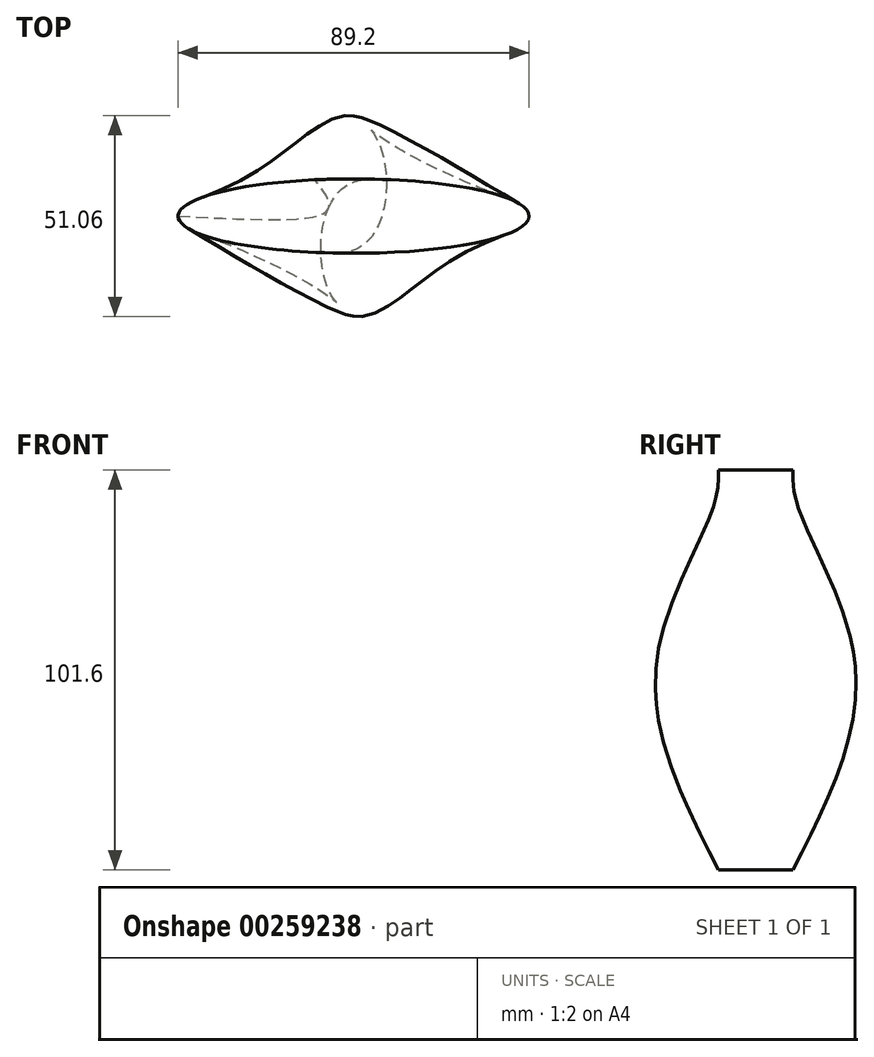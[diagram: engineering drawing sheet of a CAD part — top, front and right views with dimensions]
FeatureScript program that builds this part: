
annotation { "Feature Type Name" : "Feature", "Feature Type Description" : "" }
export const myFeature = defineFeature(function(context is Context, id is Id, definition is map)
    precondition{}
    {
        {
            var Q0;
            Q0=qCreatedBy(makeId("Top.planeOp"),FACE);
            var sketch = newSketch(context, id + "F0", { "sketchPlane" : qUnion([Q0])});
            skEllipse(sketch, "E0", {"center": v(0, 0) * mm, "majorRadius": 44.6 * mm, "minorRadius": 9.45 * mm, "majorAxis": v(-1, 0)});
            skSolve(sketch);
        }
        {
            var Q0;
            Q0=qCreatedBy(makeId("Top.planeOp"),FACE);
            cPlane(context, id + "F1", {"entities" : qUnion([Q0]), "cplaneType" : CPlaneType.OFFSET, "offset" : 50.8 * mm, "width" : 152.4 * mm, "height" : 152.4 * mm});
        }
        {
            var Q0;
            Q0=qCreatedBy(id+"F1.planeOp",FACE);
            var sketch = newSketch(context, id + "F2", { "sketchPlane" : qUnion([Q0])});
            skEllipse(sketch, "E1.0", {"center": v(0, 0) * mm, "majorRadius": 25.4 * mm, "minorRadius": 9.45 * mm, "majorAxis": v(0, 1)});
            skEllipse(sketch, "E2.0.0", {"center": v(0, 0) * mm, "majorRadius": 44.6 * mm, "minorRadius": 9.45 * mm, "majorAxis": v(-1, 0), "construction": true});
            skSolve(sketch);
        }
        {
            var Q0;
            Q0=qCreatedBy(id+"F1.planeOp",FACE);
            cPlane(context, id + "F3", {"entities" : qUnion([Q0]), "cplaneType" : CPlaneType.OFFSET, "offset" : 50.8 * mm, "width" : 152.4 * mm, "height" : 152.4 * mm});
        }
        {
            var Q0;
            Q0=qCreatedBy(id+"F3.planeOp",FACE);
            var sketch = newSketch(context, id + "F4", { "sketchPlane" : qUnion([Q0])});
            skEllipse(sketch, "E3.0", {"center": v(0, 0) * mm, "majorRadius": 44.6 * mm, "minorRadius": 9.45 * mm, "majorAxis": v(-1, 0)});
            skSolve(sketch);
        }
        {
            var Q0;
            Q0=makeQuery(id+"F0.imprint","IMPRINT",FACE,{"disambiguationData":[TD([[makeQuery(id+"F0.imprint","IMPRINT",EDGE,{"derivedFrom":sQuery(id+"F0.wireOp",EDGE,"E0")}),1.0]])]});
            var Q1;
            Q1=makeQuery(id+"F2.imprint","IMPRINT",FACE,{"disambiguationData":[TD([[makeQuery(id+"F2.imprint","IMPRINT",EDGE,{"derivedFrom":sQuery(id+"F2.wireOp",EDGE,"E1.0")}),1.0]])]});
            var Q2;
            Q2=makeQuery(id+"F4.imprint","IMPRINT",FACE,{"disambiguationData":[TD([[makeQuery(id+"F4.imprint","IMPRINT",EDGE,{"derivedFrom":sQuery(id+"F4.wireOp",EDGE,"E3.0")}),1.0]])]});
            loft(context, id + "F5", {"sheetProfilesArray" : [{ "sheetProfileEntities" : qUnion([Q0]) }, { "sheetProfileEntities" : qUnion([Q1]) }, { "sheetProfileEntities" : qUnion([Q2]) }]});
        }
    });
